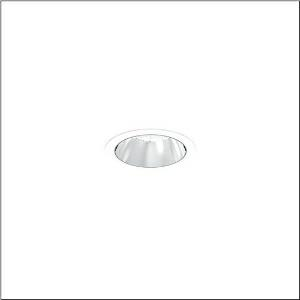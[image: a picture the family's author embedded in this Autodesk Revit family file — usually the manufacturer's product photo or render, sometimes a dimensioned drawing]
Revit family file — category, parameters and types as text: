
# Revit family: lunis_21_m_51db15tc91c
name_source: partatom
category: Lighting Fixtures
units: mm (PartAtom-declared; Revit-internal decimal feet)

## family parameters
Cut with Voids When Loaded = No
Host = Face
Light Source = No
Part Type = Normal
Room Calculation Point = No
Round Connector Dimension = Use Diameter
Shared = No

## types (1)
- --- (1 x LED 3000 K ... 6500 K, 3950 lm, 26 W, 4000K)
    Apparent Load = 26 VA
    CIE Flux Codes = 95 99 100 100 100
    Color Rendering = 80
    Color Temperature = 4000K
    Default Elevation = 1800 mm
    Description = Lunis 21,  M, downlight, light control with lens, of PMMA, anti glare with reflector, of aluminium, highly specular, light emission: direct distribution, LED rated luminous flux: 3.950lm, light colour: 8tw, with terminal, 5-pole, mains connection: 220..240V, AC/DC, 0/50..60Hz, housing, round, of diecast aluminium, traffic white (RAL 9016), diameter: 115mm, clamping range: 1..40mm, protection rating (complete): IP20, protection rating (on room side): IP54, insulation class (complete): insulation class II (safety insulation), certification: CE, impact resistance: IK03, packaging unit: 1 piece
    Height = 0 mm  [stored 0 ft]
    Lamp = 1 x LED 3000 K ... 6500 K
    Lamp Light Flux = 3950 lm
    Lamp Power = 26 W
    Lamp count = 1
    Length = 115 mm
    Luminous efficacy = 152 lm/W
    Manufacturer = Siteco
    ModVariant = No
    Model = 51DB15TC91C
    Mounting Place = Ceiling
    Mounting Type = Recessed
    Number of Poles = 1
    OnlyDefault = Yes
    Power Factor = 1
    Product Name = Lunis 21 M
    Product group = downlight
    ProductGroupID = 400
    Protection Class = Protection class II
    Protection Degree = IP 20
    RLX_Detail_Level = 1
    RLX_Emergency_Light_Flux = 0 lm
    RLX_Emergency_Type = 0
    RLX_Emergency_Type_DB = No
    RlxData = <blob elided: 11269 chars, md5=9cb63e1f>
    Socket = socket
    Standby Power = 0 W
    System Light Flux = 3950 lm
    System Power = 26 W
    Type Comments = individual setting: CCT=4000K, colour temperature 4000K, luminous flux: 100 % | (ON | ON | OFF | OFF) | 700 mA
    Type Image = l_1290850.jpg
    URL = http://relux.com
    VarID = @adj_020544
    Voltage = 0 V
    Weight = 0.00 kg
    Width = 0 mm  [stored 0 ft]

note: [stored X ft] marks values corroborated as IEEE doubles in the binary element streams (Revit-internal decimal feet)

## geometry (parser evidence)
native form markers: Sweep x9
no freeform markers — native parametric forms only
